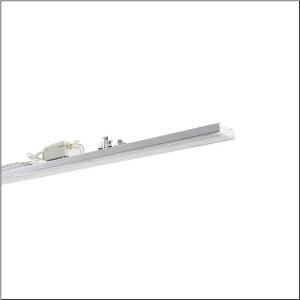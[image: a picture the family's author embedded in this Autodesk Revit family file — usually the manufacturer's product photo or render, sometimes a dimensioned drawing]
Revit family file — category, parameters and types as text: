
# Revit family: licross_21_recessed_mo_52tl18vn58xg
name_source: partatom
category: Lighting Fixtures
units: mm (PartAtom-declared; Revit-internal decimal feet)

## family parameters
Cut with Voids When Loaded = No
Host = Face
Light Source = No
Part Type = Normal
Room Calculation Point = No
Round Connector Dimension = Use Diameter
Shared = No

## types (1)
- --- (1 x LED, 8000 lm, 46.1 W, 5000K)
    Apparent Load = 46 VA
    CIE Flux Codes = 79 95 99 100 100
    Color Rendering = 80
    Color Temperature = 5000K
    Default Elevation = 1800 mm
    Description = Licross 21 Recessed MO, luminaire insert, of sheet steel, galvanised, coil coated, white, length: 1.500mm, width: 66mm, height: 67mm, LED rated luminous flux: 8.000lm, light colour: 850, SDCM (Standard Deviation of Colour Matching)MacAdam ≤ 3 SDCM (initial), control gear: DALI 2, CLO, with plug, 5-pole, with phase selection, mains connection: 220..240V, AC, 50/60Hz, start of lifetime: 46W, end of service life: 55W, internal wiring halogen-free, primary optical cover: cover, of PMMA, light emission: direct distribution, primary light characteristic: symmetric, protection rating (complete): IP40, insulation class (complete): insulation class I (protective earthing), certification: CE, ENEC, VDE, UKCA, protection symbol: D if used in an environment without relevant dust loads with corresponding accessories, impact resistance: IK06, permissible ambient temperature for indoor applications: -25..+40°C, corresponds to IFS (International Featured Standards) requirements for safety and quality in the food industry, reducing of maximum allowable ambient temperature of 5°C with ceiling mounting, LABS conformity tested according to VDMA 24364:2018-05, The light source and the operating device comply with the requirements of the Ecodesign Regulation (EU) 2019/2020 and are replaceable in accordance with this regulation, packaging unit: 1 piece
    Height = 58 mm
    Lamp = 1 x LED
    Lamp Light Flux = 8000 lm
    Lamp Power = 46.1 W
    Lamp count = 1
    Length = 1500 mm
    Luminous efficacy = 174 lm/W
    Manufacturer = Siteco
    ModVariant = No
    Model = 52TL18VN58XG
    Mounting Place = Ceiling
    Mounting Type = Pendant
    Number of Poles = 1
    OnlyDefault = Yes
    Power Factor = 1
    Product Name = Licross 21 Recessed MO
    Product group = luminaire insert | ceiling pendant
    ProductGroupID = 901
    Protection Class = Protection class I
    Protection Degree = IP 40
    RLX_Detail_Level = 1
    RLX_Emergency_Light_Flux = 0 lm
    RLX_Emergency_Type = 0
    RLX_Emergency_Type_DB = No
    RlxData = <blob elided: 24845 chars, md5=bf5e7e5d>
    Socket = socket
    Standby Power = 0 W
    System Light Flux = 8000 lm
    System Power = 46 W
    Type Comments = factory setting: luminous flux: 100 % | dim-lin: 254 | 310 mA
    Type Image = l_1296930.jpg
    URL = http://relux.com
    VarID = @adj_088759
    Voltage = 0 V
    Weight = 0.00 kg
    Width = 66 mm

## geometry (parser evidence)
native form markers: Blend x4, Sweep x13
no freeform markers — native parametric forms only
